# Revit family: QF_T&S_B-0155-LN
name_source: partatom
category: Specialty Equipment
revit_build: Autodesk Revit 2015 (Build: 20140606_1530(x64)
units: mm (PartAtom-declared; Revit-internal decimal feet)

## types (1)
- QF_T&S_B-0155-LN
    Cold Water Connection Height = 0"
    Cold Water Consumption = 9.460 GPM
    Cold Water Flow = 9.46 GPM
    Cold Water Inlet Flow = 9.46 GPM
    Cold Water Maximum Pressure = 125.00 psi
    Cold Water Minimum Pressure = 20.00 psi
    Cold Water RI Height = 0"
    Cold Water Size = 0"
    Cold Water Temperature Recommended = 40 °F
    Connector 1 Description = Cold Water Inlet
    Connector 2 Description = Hot Water Inlet
    Description = Add-On Faucet w/ 1/4 Turn Eterna Cartridge & Lever Handle (Less Nozzle)
    Faucet Material = QF_Metal-Stainless-Polished
    Hot Water Connection Height = 0"
    Hot Water Consumption = 9.46 GPM
    Hot Water Inlet Flow = 9.46 GPM
    Hot Water Maximum Pressure = 125.00 psi
    Hot Water Minimum Pressure = 20.00 psi
    Hot Water RI Height = 0"
    Hot Water Size = 0"
    Hot Water Temperature = 140 °F
    Manufacturer = T&S Brass and Bronze Works, Inc.
    Model = B-0155-LN
    Plumbing Remarks = Pressure: 20 - 125 psi, Temperature: 40°F - 140°F, Flow Rate: 9.46 GPM @ 60 psi. Outlet device &/or final configuration may reduce flow rate.
    Product Documentation Link = http://catalog.tsbrass.com
    URL = http://www.tsbrass.com
    Water Supply Radius = 3/16"
    Weight in Pounds = 0

## geometry (parser evidence)
native form markers: Blend x52, Sweep x4
no freeform markers — native parametric forms only
